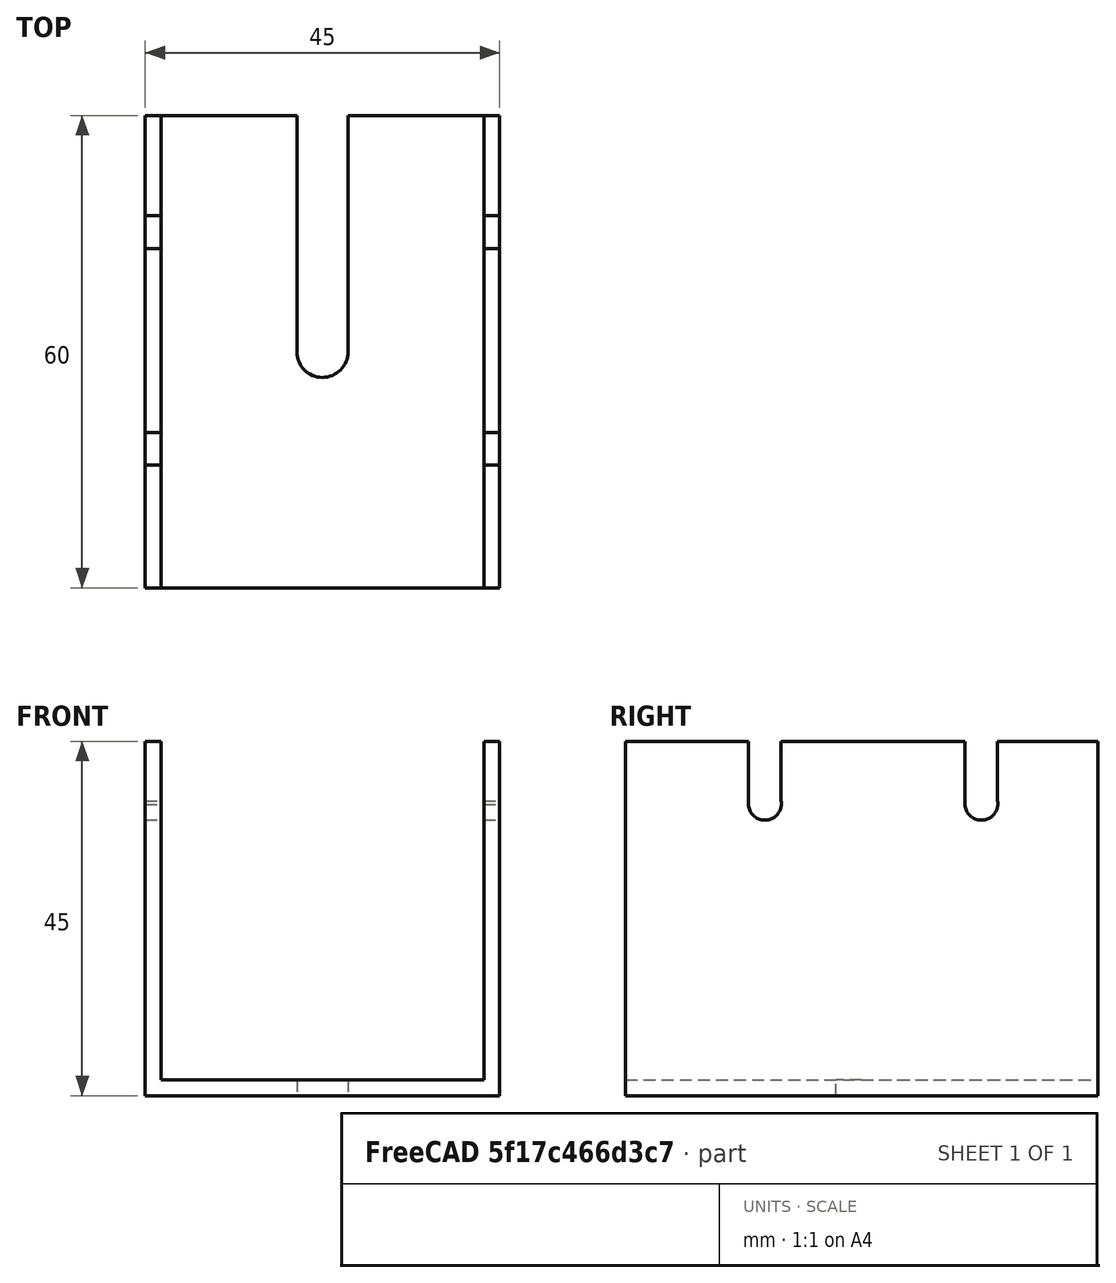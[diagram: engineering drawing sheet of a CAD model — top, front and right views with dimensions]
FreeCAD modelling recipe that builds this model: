
FCSTD DOCUMENT  (FreeCAD 0.15R4671 (Git))
Label: sujeccion superior aluminio
License: All rights reserved
LicenseURL: http://es.wikipedia.org/wiki/Todos_los_derechos_reservados
objects: Part::Box×5, Part::MultiFuse×4, Part::Cylinder×2, Part::FeaturePython×2, Part::Cut×1
note: 14 computed .brp shape members not serialized (recipe doc carries the construction recipe); baked Part::Feature solids carry a one-line shape summary decoded from their .brp

FEATURE [Part::Box] Box  label="pared inferior"
  Height = 2
  Length = 45
  Width = 60
FEATURE [Part::Box] Box001  label="pared derecha"
  Height = 45
  Length = 2
  Width = 60
FEATURE [Part::Box] Box002  label="pared izquierda"
  Height = 45
  Length = 2
  Placement = pos=(43,0,0) rot=(0,0,1;0rad)
  Width = 60
FEATURE [Part::MultiFuse] Fusion
  Shapes = -> [Box001,Box,Box002]
FEATURE [Part::Cylinder] Cylinder  label="Cilindro"
  Angle = 360
  Height = 2
  Placement = pos=(0,17.7,37.1) rot=(0,1,0;1.5708rad)
  Radius = 2.1
FEATURE [Part::FeaturePython] Array  # Draft array (typed FeaturePython)
  Angle = 360
  ArrayType = 0
  Axis = (0,0,1)
  Base = -> Cylinder
  Center = (0,0,0)
  Fuse = false
  IntervalAxis = (0,0,0)
  IntervalX = (43,0,0)
  IntervalY = (0,27.5,0)
  IntervalZ = (0,0,0)
  NumberPolar = 1
  NumberX = 2
  NumberY = 2
  NumberZ = 1
FEATURE [Part::Box] Box003  label="Cubo"
  Height = 13
  Length = 2
  Placement = pos=(0,15.6,37) rot=(0,0,1;0rad)
  Width = 4.17
FEATURE [Part::FeaturePython] Array001  # Draft array (typed FeaturePython)
  Angle = 360
  ArrayType = 0
  Axis = (0,0,1)
  Base = -> Box003
  Center = (0,0,0)
  Fuse = false
  IntervalAxis = (0,0,0)
  IntervalX = (43,0,0)
  IntervalY = (0,27.5,0)
  IntervalZ = (0,0,0)
  NumberPolar = 1
  NumberX = 2
  NumberY = 2
  NumberZ = 1
FEATURE [Part::Cylinder] Cylinder001  label="Cilindro001"
  Angle = 360
  Height = 2
  Placement = pos=(22.5,30,0) rot=(0,0,1;0rad)
  Radius = 3.25
FEATURE [Part::Box] Box004  label="Cubo001"
  Height = 2
  Length = 6.5
  Placement = pos=(19.25,30,0) rot=(0,0,1;0rad)
  Width = 36
FEATURE [Part::MultiFuse] Fusion001
  Shapes = -> [Box004,Cylinder001]
FEATURE [Part::MultiFuse] Fusion002
  Shapes = -> [Array,Array001]
FEATURE [Part::MultiFuse] Fusion003
  Shapes = -> [Fusion001,Fusion002]
FEATURE [Part::Cut] Cut
  Base = -> Fusion
  Tool = -> Fusion003
